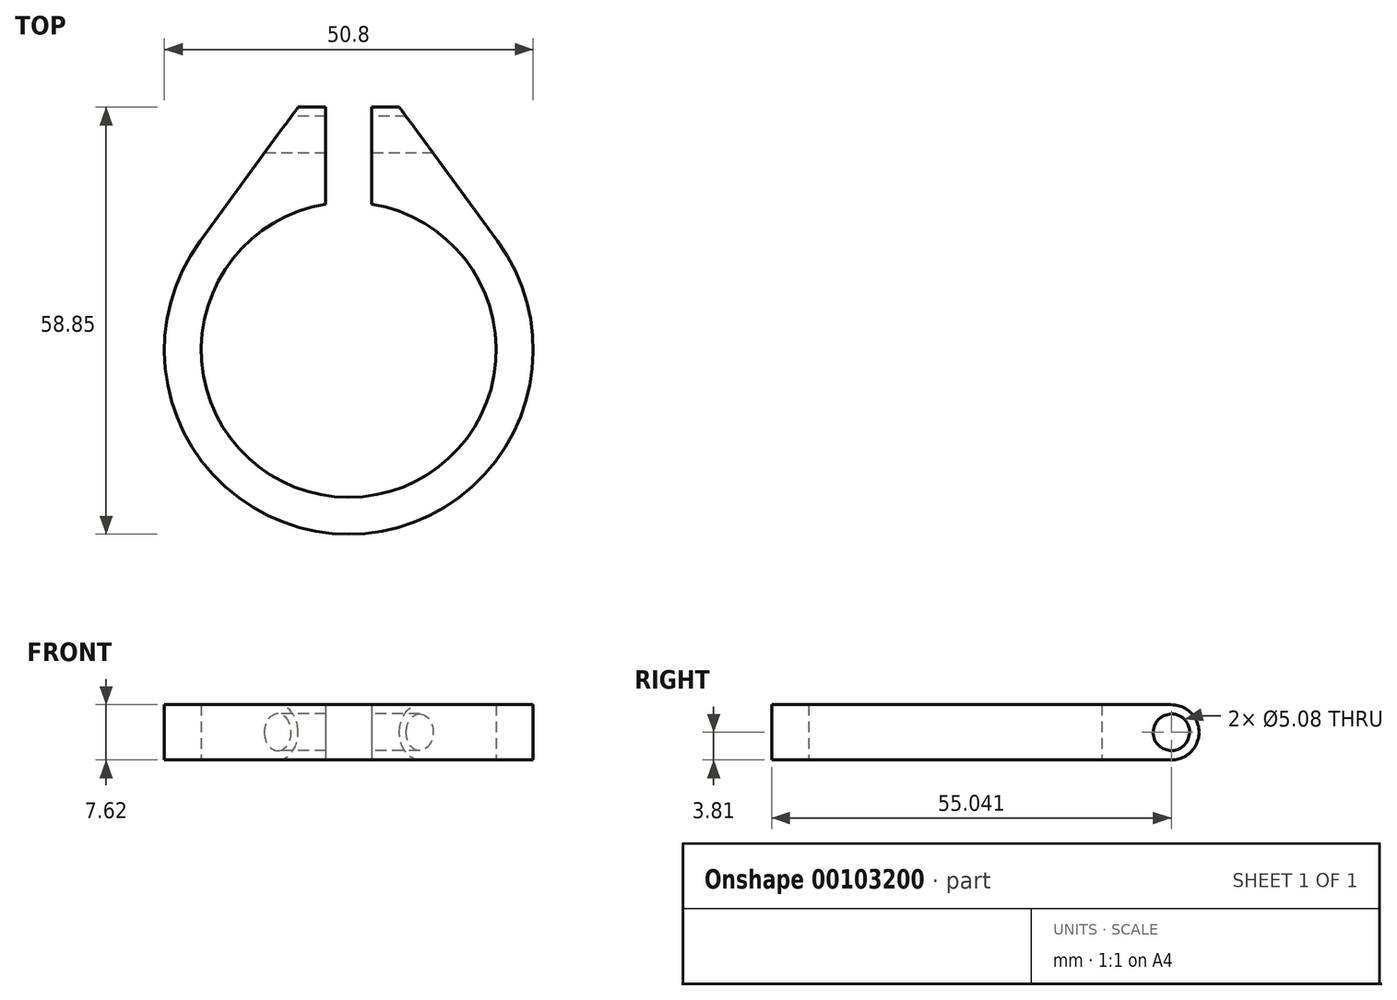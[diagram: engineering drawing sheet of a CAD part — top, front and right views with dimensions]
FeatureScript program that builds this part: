
annotation { "Feature Type Name" : "Feature", "Feature Type Description" : "" }
export const myFeature = defineFeature(function(context is Context, id is Id, definition is map)
    precondition{}
    {
        {
            var Q0;
            Q0=qCreatedBy(makeId("Top.planeOp"),FACE);
            var sketch = newSketch(context, id + "F0", { "sketchPlane" : qUnion([Q0])});
            skArc(sketch, "E0", {"start": v(-3.18, 20.07) * mm, "mid": v(0, -20.32) * mm, "end": v(3.18, 20.07) * mm});
            skArc(sketch, "E1", {"start": v(-20.5, 15) * mm, "mid": v(0, -25.4) * mm, "end": v(20.5, 15) * mm});
            skLineSegment(sketch, "E2", {"start": v(-3.18, 20.07) * mm, "end": v(-3.18, 33.45) * mm});
            skLineSegment(sketch, "E3", {"start": v(-3.18, 33.45) * mm, "end": v(-6.99, 33.45) * mm});
            skLineSegment(sketch, "E4", {"start": v(-6.99, 33.45) * mm, "end": v(-20.5, 15) * mm});
            skLineSegment(sketch, "E5.MirrorCS", {"start": v(3.18, 33.45) * mm, "end": v(6.99, 33.45) * mm});
            skLineSegment(sketch, "E6.MirrorCS", {"start": v(6.99, 33.45) * mm, "end": v(20.5, 15) * mm});
            skLineSegment(sketch, "E7.MirrorCS", {"start": v(3.18, 20.07) * mm, "end": v(3.18, 33.45) * mm});
            skSolve(sketch);
        }
        {
            var Q0;
            Q0=makeQuery(id+"F0.imprint","IMPRINT",FACE,{"disambiguationData":[TD([[makeQuery(id+"F0.imprint","IMPRINT",EDGE,{"derivedFrom":sQuery(id+"F0.wireOp",EDGE,"E0")}),-1.0]])]});
            extrude(context, id + "F1", {"entities" : qUnion([Q0]), "depth" : 7.62 * mm});
        }
        {
            var Q0;
            Q0=makeQuery(id+"F1.opExtrude","SWEPT_FACE",FACE,{"disambiguationData":[OSD([sQuery(id+"F0.wireOp",EDGE,"E2")])]});
            var sketch = newSketch(context, id + "F2", { "sketchPlane" : qUnion([Q0])});
            skCircle(sketch, "E8", {"center": v(29.64, 3.81) * mm, "radius": 2.54 * mm});
            skPoint(sketch, "E8.centerSnap0", {"position": v(33.45, 3.81) * mm});
            skSolve(sketch);
        }
        {
            var Q0;
            Q0=makeQuery(id+"F2.imprint","IMPRINT",FACE,{"disambiguationData":[TD([[makeQuery(id+"F2.imprint","IMPRINT",EDGE,{"derivedFrom":sQuery(id+"F2.wireOp",EDGE,"E8")}),1.0]])]});
            extrude(context, id + "F3", {"entities" : qUnion([Q0]), "operationType" : NewBodyOperationType.REMOVE, "depth" : 25.4 * mm, "hasSecondDirection" : true, "secondDirectionOppositeDirection" : true, "secondDirectionDepth" : 25.4 * mm});
        }
        {
            var Q0;
            Q0=makeQuery(id+"F1.opExtrude","CAP_EDGE",EDGE,{"disambiguationData":[OSD([sQuery(id+"F0.wireOp",EDGE,"E3")])],"isStart":true});
            var Q1;
            Q1=makeQuery(id+"F1.opExtrude","CAP_EDGE",EDGE,{"disambiguationData":[OSD([sQuery(id+"F0.wireOp",EDGE,"E5.MirrorCS")])],"isStart":true});
            fillet(context, id + "F4", {"entities" : qUnion([Q0, Q1]), "radius" : 3.8 * mm, "tangentPropagation" : true, "allowEdgeOverflow" : false});
        }
        {
            var Q0;
            Q0=makeQuery(id+"F1.opExtrude","CAP_EDGE",EDGE,{"disambiguationData":[OSD([sQuery(id+"F0.wireOp",EDGE,"E3")])],"isStart":false});
            var Q1;
            Q1=makeQuery(id+"F1.opExtrude","CAP_EDGE",EDGE,{"disambiguationData":[OSD([sQuery(id+"F0.wireOp",EDGE,"E5.MirrorCS")])],"isStart":false});
            fillet(context, id + "F5", {"entities" : qUnion([Q0, Q1]), "radius" : 3.8 * mm, "tangentPropagation" : true, "allowEdgeOverflow" : false});
        }
    });
